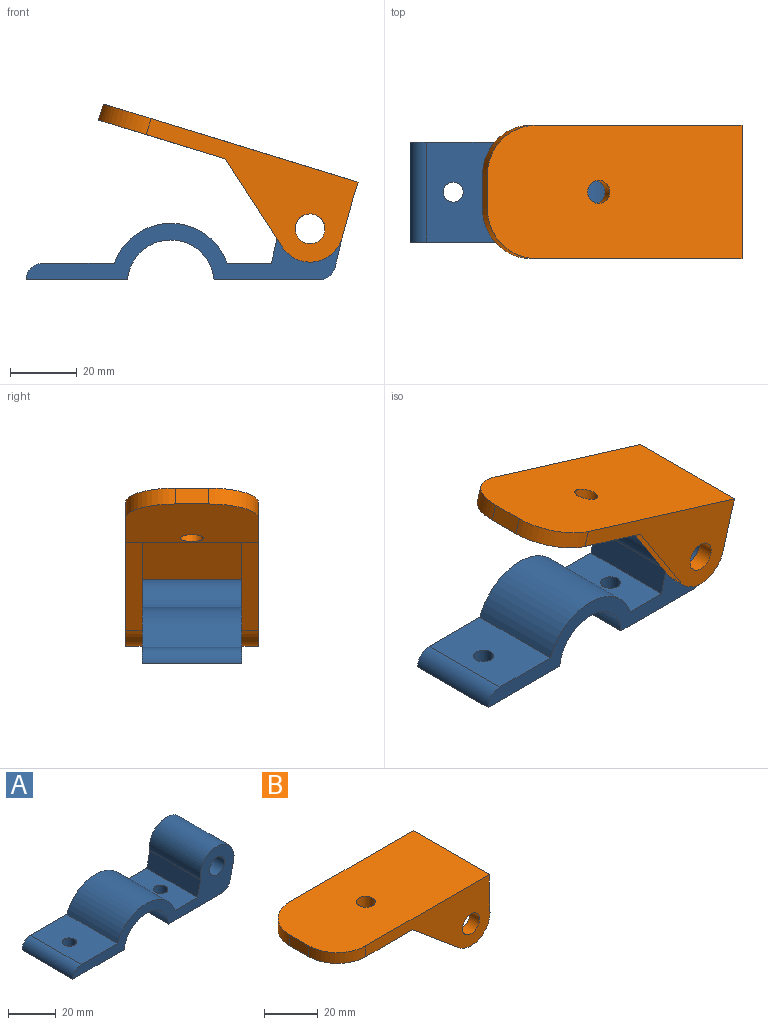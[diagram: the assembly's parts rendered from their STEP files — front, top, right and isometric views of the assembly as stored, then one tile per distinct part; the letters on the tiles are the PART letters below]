
ASSEMBLY  parts=2 mates=1
PART A: 16 faces, bbox 95.3x30x25.4 mm
  f0: plane 30x21.51mm, normal (0,0,1), area 616.9mm2, adj f9,f10,f11,f13,f15
  f1: plane 30.5x30mm, normal (0,0,-1), area 886.7mm2, adj f2,f10,f11,f13,f15
  f2: cylinder r=13.04mm len=30mm, axis (0,1,0), area 1167.3mm2, adj f1,f3,f10,f11
  f3: plane 31.56x30mm, normal (0,0,-1), area 918.5mm2, adj f2,f10,f11,f12,f14
  f4: plane 30x9.21mm, normal (0.97,0,-0.23), area 283.8mm2, adj f5,f10,f11,f14
  f5: cylinder r=10mm len=30mm, axis (0,1,0), area 1080.5mm2, adj f4,f6,f10,f11
  f6: plane 30x8.07mm, normal (-0.97,0,0.23), area 248.6mm2, adj f5,f7,f10,f11
  f7: plane 30x13.23mm, normal (0,0,1), area 368.6mm2, adj f6,f9,f10,f11,f12
  f8: cylinder r=4.5mm len=30mm, axis (0,1,0), area 848.2mm2, adj f10,f11
  f9: cylinder r=18.03mm len=33.99mm, axis (0,1,0), area 1330.9mm2, adj f0,f7,f10,f11
  f10: plane 95.35x25.35mm, normal (0,-1,0), area 807.7mm2, adj f0,f1,f2,f3,f4,f5,f6,f7
  f11: plane 95.35x25.35mm, normal (0,1,0), area 807.7mm2, adj f0,f1,f2,f3,f4,f5,f6,f7
  f12: cylinder r=3mm len=6mm, axis (0,0,1), area 94.2mm2, adj f3,f7
  f13: cylinder r=3mm len=6mm, axis (0,0,1), area 94.2mm2, adj f0,f1
  f14: cylinder r=5mm len=30mm, axis (0,1,0), area 201.1mm2, adj f3,f4,f10,f11
  f15: cylinder r=5mm len=30mm, axis (0,1,0), area 235.6mm2, adj f0,f1,f10,f11
PART B: 18 faces, bbox 80.3x40x27.7 mm
  f0: cylinder r=10mm len=16.43mm, axis (0,1,0), area 114.8mm2, adj f4,f6,f11,f14
  f1: cylinder r=4.5mm len=9mm, axis (0,1,0), area 141.4mm2, adj f11,f14
  f2: plane 10x5mm, normal (-1,0,0), area 50mm2, adj f3,f8,f15,f16
  f3: plane 40x39.69mm, normal (0,0,-1), area 1452.5mm2, adj f2,f4,f10,f11,f15,f16,f17
  f4: plane 40x24.22mm, normal (-0.64,0,-0.77), area 316.3mm2, adj f0,f3,f5,f10,f11,f12,f13,f14
  f5: cylinder r=10mm len=16.43mm, axis (0,1,0), area 114.8mm2, adj f4,f6,f10,f13
  f6: plane 40x12.41mm, normal (1,0,0.03), area 124.7mm2, adj f0,f5,f7,f10,f11,f12,f13,f14
  f7: plane 40x5mm, normal (1,0,0), area 200mm2, adj f6,f8,f10,f11
  f8: plane 80x40mm, normal (0,0,1), area 3064.9mm2, adj f2,f7,f10,f11,f15,f16,f17
  f9: cylinder r=4.5mm len=9mm, axis (0,1,0), area 141.4mm2, adj f10,f13
  f10: plane 65.33x27.68mm, normal (0,-1,0), area 852mm2, adj f3,f4,f5,f6,f7,f8,f9,f16
  f11: plane 65.33x27.68mm, normal (0,1,0), area 852mm2, adj f0,f1,f3,f4,f6,f7,f8,f15
  f12: plane 40.31x30mm, normal (0,0,-1), area 1209.3mm2, adj f4,f6,f13,f14
  f13: plane 40.64x22.68mm, normal (0,1,0), area 526.6mm2, adj f4,f5,f6,f9,f12
  f14: plane 40.64x22.68mm, normal (0,-1,0), area 526.6mm2, adj f0,f1,f4,f6,f12
  f15: cylinder r=15mm len=15mm, axis (0,0,-1), area 117.8mm2, adj f2,f3,f8,f11
  f16: cylinder r=15mm len=15mm, axis (0,0,1), area 117.8mm2, adj f2,f3,f8,f10
  f17: cylinder r=3.5mm len=7mm, axis (0,0,1), area 110mm2, adj f3,f8
PLACE A t=(-3.08,-5,-0.81)mm fixed
PLACE B rot(axis=(0,1,0),17deg) t=(-14.55,0,-9.75)mm
MATE revolute A.f5 <-> B.f0  axis (0,1,0) through (42.27,-35,14.54)mm
